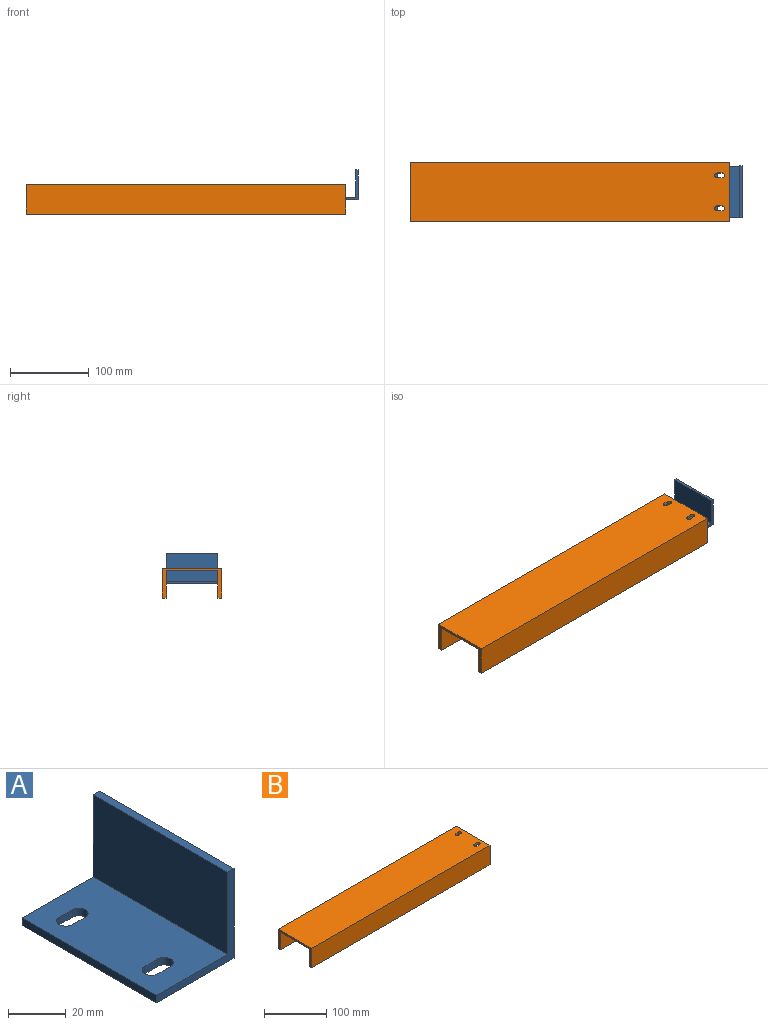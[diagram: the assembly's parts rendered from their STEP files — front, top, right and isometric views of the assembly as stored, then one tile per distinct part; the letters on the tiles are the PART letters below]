
ASSEMBLY  parts=2 mates=1
PART A: 16 faces, bbox 38.1x66x38.1 mm
  f0: plane 66.04x34.93mm, normal (0,0,1), area 2162.5mm2, adj f1,f5,f6,f7,f8,f9,f10,f11
  f1: plane 66.04x3.18mm, normal (-1,0,0), area 209.7mm2, adj f0,f2,f6,f7
  f2: plane 66.04x38.1mm, normal (0,0,-1), area 2372.1mm2, adj f1,f3,f6,f7,f8,f9,f10,f11
  f3: plane 66.04x38.1mm, normal (1,0,0), area 2516.1mm2, adj f2,f4,f6,f7
  f4: plane 66.04x3.18mm, normal (0,0,1), area 209.7mm2, adj f3,f5,f6,f7
  f5: plane 66.04x34.93mm, normal (-1,0,0), area 2306.4mm2, adj f0,f4,f6,f7
  f6: plane 38.1x38.1mm, normal (0,-1,0), area 231.9mm2, adj f0,f1,f2,f3,f4,f5
  f7: plane 38.1x38.1mm, normal (0,1,0), area 231.9mm2, adj f0,f1,f2,f3,f4,f5
  f8: plane 6.35x3.18mm, normal (0,-1,0), area 20.2mm2, adj f0,f2,f9,f10
  f9: cylinder r=3.17mm len=6.35mm, axis (0,0,1), area 31.7mm2, adj f0,f2,f8,f11
  f10: cylinder r=3.17mm len=6.35mm, axis (0,0,1), area 31.7mm2, adj f0,f2,f8,f11
  f11: plane 6.35x3.18mm, normal (0,1,0), area 20.2mm2, adj f0,f2,f9,f10
  f12: plane 6.35x3.18mm, normal (0,-1,0), area 20.2mm2, adj f0,f2,f13,f14
  f13: cylinder r=3.17mm len=6.35mm, axis (0,0,1), area 31.7mm2, adj f0,f2,f12,f15
  f14: cylinder r=3.17mm len=6.35mm, axis (0,0,1), area 31.7mm2, adj f0,f2,f12,f15
  f15: plane 6.35x3.18mm, normal (0,1,0), area 20.2mm2, adj f0,f2,f13,f14
PART B: 18 faces, bbox 406.4x76.2x38.1 mm
  f0: plane 406.4x66.04mm, normal (0,0,-1), area 26694.7mm2, adj f4,f5,f8,f9,f10,f11,f12,f13
  f1: plane 406.4x76.2mm, normal (0,0,1), area 30823.7mm2, adj f2,f7,f8,f9,f10,f11,f12,f13
  f2: plane 406.4x38.1mm, normal (0,-1,0), area 15483.8mm2, adj f1,f3,f8,f9
  f3: plane 406.4x5.08mm, normal (0,0,-1), area 2064.5mm2, adj f2,f4,f8,f9
  f4: plane 406.4x34.8mm, normal (0,1,0), area 14141.9mm2, adj f0,f3,f8,f9
  f5: plane 406.4x34.8mm, normal (0,-1,0), area 14141.9mm2, adj f0,f6,f8,f9
  f6: plane 406.4x5.08mm, normal (0,0,-1), area 2064.5mm2, adj f5,f7,f8,f9
  f7: plane 406.4x38.1mm, normal (0,1,0), area 15483.8mm2, adj f1,f6,f8,f9
  f8: plane 76.2x38.1mm, normal (1,0,0), area 605.2mm2, adj f0,f1,f2,f3,f4,f5,f6,f7
  f9: plane 76.2x38.1mm, normal (-1,0,0), area 605.2mm2, adj f0,f1,f2,f3,f4,f5,f6,f7
  f10: cylinder r=3.17mm len=6.35mm, axis (0,0,1), area 32.9mm2, adj f0,f1,f11,f13
  f11: plane 6.35x3.3mm, normal (0,1,0), area 21mm2, adj f0,f1,f10,f12
  f12: cylinder r=3.17mm len=6.35mm, axis (0,0,1), area 32.9mm2, adj f0,f1,f11,f13
  f13: plane 6.35x3.3mm, normal (0,-1,0), area 21mm2, adj f0,f1,f10,f12
  f14: plane 6.35x3.3mm, normal (0,-1,0), area 21mm2, adj f0,f1,f15,f16
  f15: cylinder r=3.17mm len=6.35mm, axis (0,0,1), area 32.9mm2, adj f0,f1,f14,f17
  f16: cylinder r=3.17mm len=6.35mm, axis (0,0,1), area 32.9mm2, adj f0,f1,f14,f17
  f17: plane 6.35x3.3mm, normal (0,1,0), area 21mm2, adj f0,f1,f15,f16
PLACE A t=(203.64,60.86,-6.77)mm
PLACE B t=(-12.13,60.86,-2.96)mm
MATE planar A.f6 <-> B.f4  axis (0,-1,0) through (196.12,27.84,-12.07)mm
